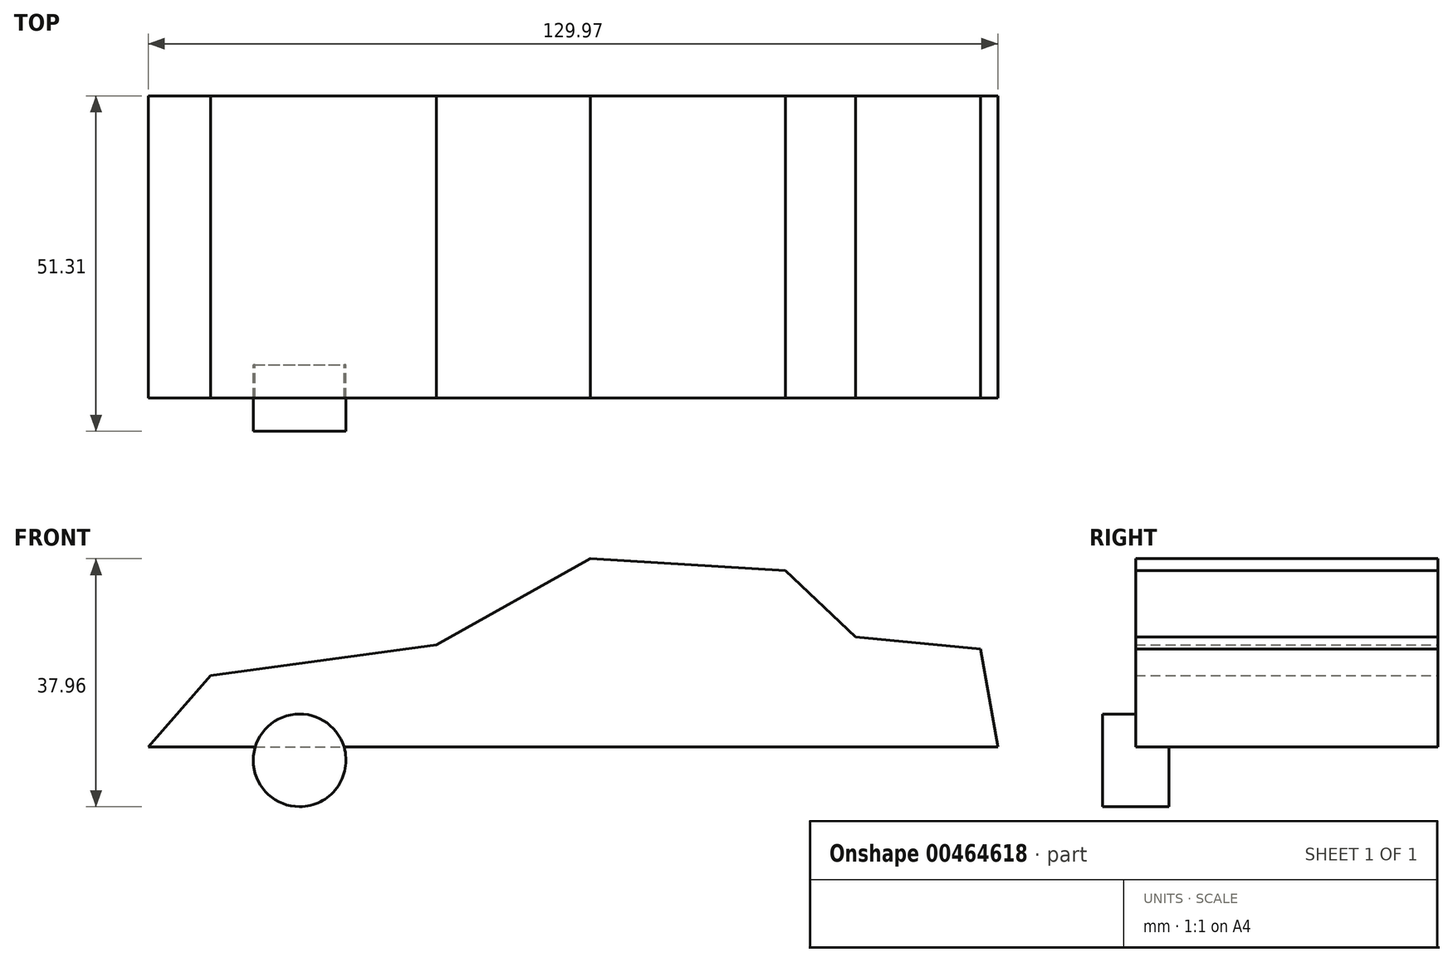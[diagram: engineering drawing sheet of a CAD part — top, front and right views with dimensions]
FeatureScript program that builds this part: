
annotation { "Feature Type Name" : "Feature", "Feature Type Description" : "" }
export const myFeature = defineFeature(function(context is Context, id is Id, definition is map)
    precondition{}
    {
        {
            var Q0;
            Q0=qCreatedBy(makeId("Front.planeOp"),FACE);
            var sketch = newSketch(context, id + "F0", { "sketchPlane" : qUnion([Q0])});
            skLineSegment(sketch, "E0", {"start": v(-62.55, 0) * mm, "end": v(-53, 10.97) * mm});
            skLineSegment(sketch, "E1", {"start": v(-53, 10.97) * mm, "end": v(-18.48, 15.64) * mm});
            skLineSegment(sketch, "E2", {"start": v(-18.48, 15.64) * mm, "end": v(5.08, 28.84) * mm});
            skLineSegment(sketch, "E3", {"start": v(5.08, 28.84) * mm, "end": v(34.93, 27) * mm});
            skLineSegment(sketch, "E4", {"start": v(34.93, 27) * mm, "end": v(45.7, 16.85) * mm});
            skLineSegment(sketch, "E5", {"start": v(45.7, 16.85) * mm, "end": v(64.78, 15.03) * mm});
            skLineSegment(sketch, "E6", {"start": v(64.78, 15.03) * mm, "end": v(67.42, 0) * mm});
            skLineSegment(sketch, "E7", {"start": v(-62.55, 0) * mm, "end": v(67.42, 0) * mm});
            skSolve(sketch);
        }
        {
            var Q0;
            Q0 = qSketchRegion(id + "F0", true);
            extrude(context, id + "F1", {"entities" : qUnion([Q0]), "depth" : 46.23 * mm});
        }
        {
            var Q0;
            Q0=makeQuery(id+"F1.opExtrude","CAP_FACE",FACE,{"disambiguationData":[OSD([sQuery(id+"F0.wireOp",EDGE,"E0"),sQuery(id+"F0.wireOp",EDGE,"E1"),sQuery(id+"F0.wireOp",EDGE,"E2"),sQuery(id+"F0.wireOp",EDGE,"E3"),sQuery(id+"F0.wireOp",EDGE,"E4"),sQuery(id+"F0.wireOp",EDGE,"E5"),sQuery(id+"F0.wireOp",EDGE,"E6"),sQuery(id+"F0.wireOp",EDGE,"E7")])],"isStart":false});
            var sketch = newSketch(context, id + "F2", { "sketchPlane" : qUnion([Q0])});
            skCircle(sketch, "E8", {"center": v(-39.4, -2.03) * mm, "radius": 7.1 * mm});
            skSolve(sketch);
        }
        {
            var Q0;
            Q0 = qSketchRegion(id + "F2", true);
            extrude(context, id + "F3", {"entities" : qUnion([Q0]), "operationType" : NewBodyOperationType.ADD, "depth" : 5.08 * mm, "hasSecondDirection" : true, "secondDirectionOppositeDirection" : true, "secondDirectionDepth" : 5.08 * mm});
        }
    });
